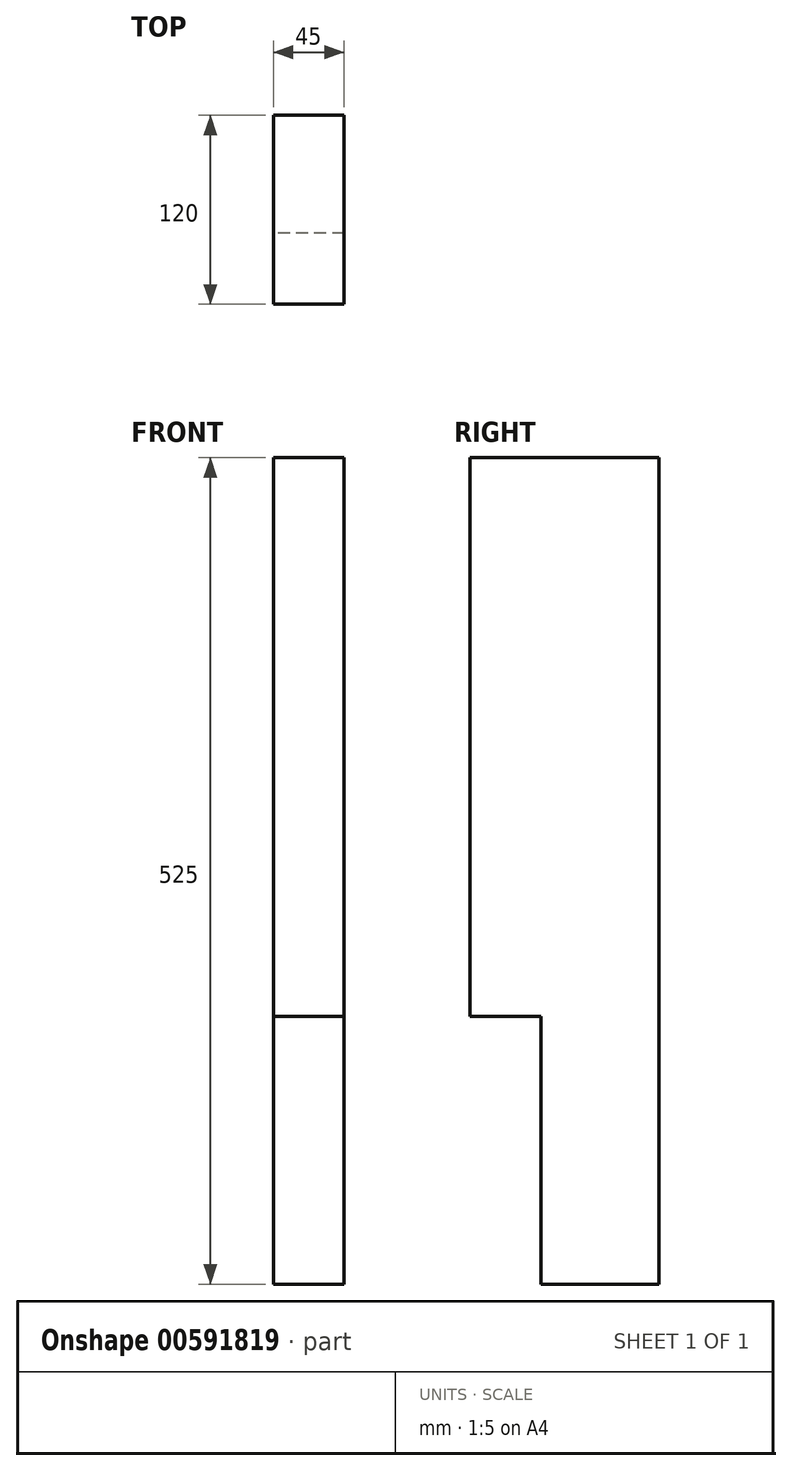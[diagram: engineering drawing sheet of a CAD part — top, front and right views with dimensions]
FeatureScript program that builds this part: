
annotation { "Feature Type Name" : "Feature", "Feature Type Description" : "" }
export const myFeature = defineFeature(function(context is Context, id is Id, definition is map)
    precondition{}
    {
        {
            var Q0;
            Q0=qCreatedBy(makeId("Right.planeOp"),FACE);
            var sketch = newSketch(context, id + "F0", { "sketchPlane" : qUnion([Q0])});
            skLineSegment(sketch, "E0.left", {"start": v(0, 0) * mm, "end": v(0, 525) * mm});
            skLineSegment(sketch, "E1.bottom", {"start": v(-120, 170) * mm, "end": v(-75, 170) * mm});
            skLineSegment(sketch, "E1.right", {"start": v(-75, 170) * mm, "end": v(-75, 0) * mm});
            skPoint(sketch, "E2.end.orphan", {"position": v(-120, 525) * mm});
            skLineSegment(sketch, "E3", {"start": v(0, 525) * mm, "end": v(-120, 525) * mm});
            skLineSegment(sketch, "E4", {"start": v(-120, 170) * mm, "end": v(-120, 525) * mm});
            skLineSegment(sketch, "E5", {"start": v(0, 0) * mm, "end": v(-75, 0) * mm});
            skSolve(sketch);
        }
        {
            var Q0;
            Q0=makeQuery(id+"F0.imprint","IMPRINT",FACE,{"disambiguationData":[TD([[makeQuery(id+"F0.imprint","IMPRINT",EDGE,{"derivedFrom":sQuery(id+"F0.wireOp",EDGE,"E0.left")}),1.0]])]});
            extrude(context, id + "F1", {"entities" : qUnion([Q0]), "depth" : 45 * mm, "offsetDistance" : 25 * mm});
        }
    });
